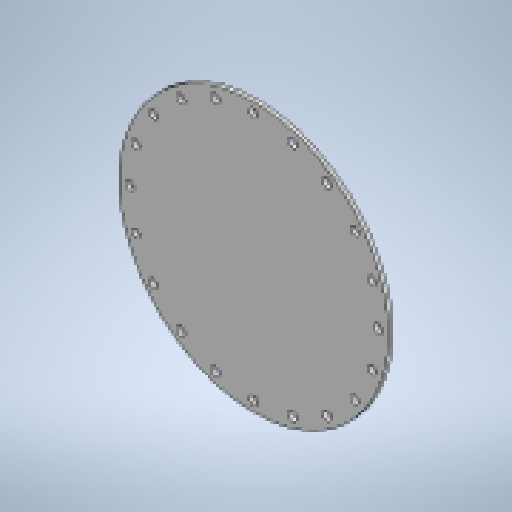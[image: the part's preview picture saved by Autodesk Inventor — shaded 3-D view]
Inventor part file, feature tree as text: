
AUTODESK INVENTOR PART (.ipt)
format: ipt  version: 2025.3 (Build 293356030, 356C)  size: 206,336 bytes
history: native  units: mm
features: sketch x2, other x2, extrude x1, pattern_circular x1
ambient origin geometry x8: Origin, YZ Plane, XZ Plane, XY Plane, X Axis, Y Axis, Z Axis, Center Point
bodies: Solid1 (feature_tree)
feature tree (6):
  extrude  "Extrusion1"  Depth=10.0mm TaperAngle=0.0deg
  pattern_circular  "Circular Pattern1"  Count=62  [1 undecoded]
  sketch  "Sketch1"  dims[d0=670.0mm d1=10.0mm d2=0.0mm]
  sketch  "Sketch2"  dims[d3=22.0mm d4=620.0mm d5=10.0mm d6=10.0mm d7=0.0mm d8=200.0mm d9=360.0deg]
  other  "Cut1"
  other  "Definition1"
note: 1 required parameter value undecoded (feature->parameter linkage not recoverable at this tier; creation-order binding heuristic only, values carry confidence <= 0.55)
